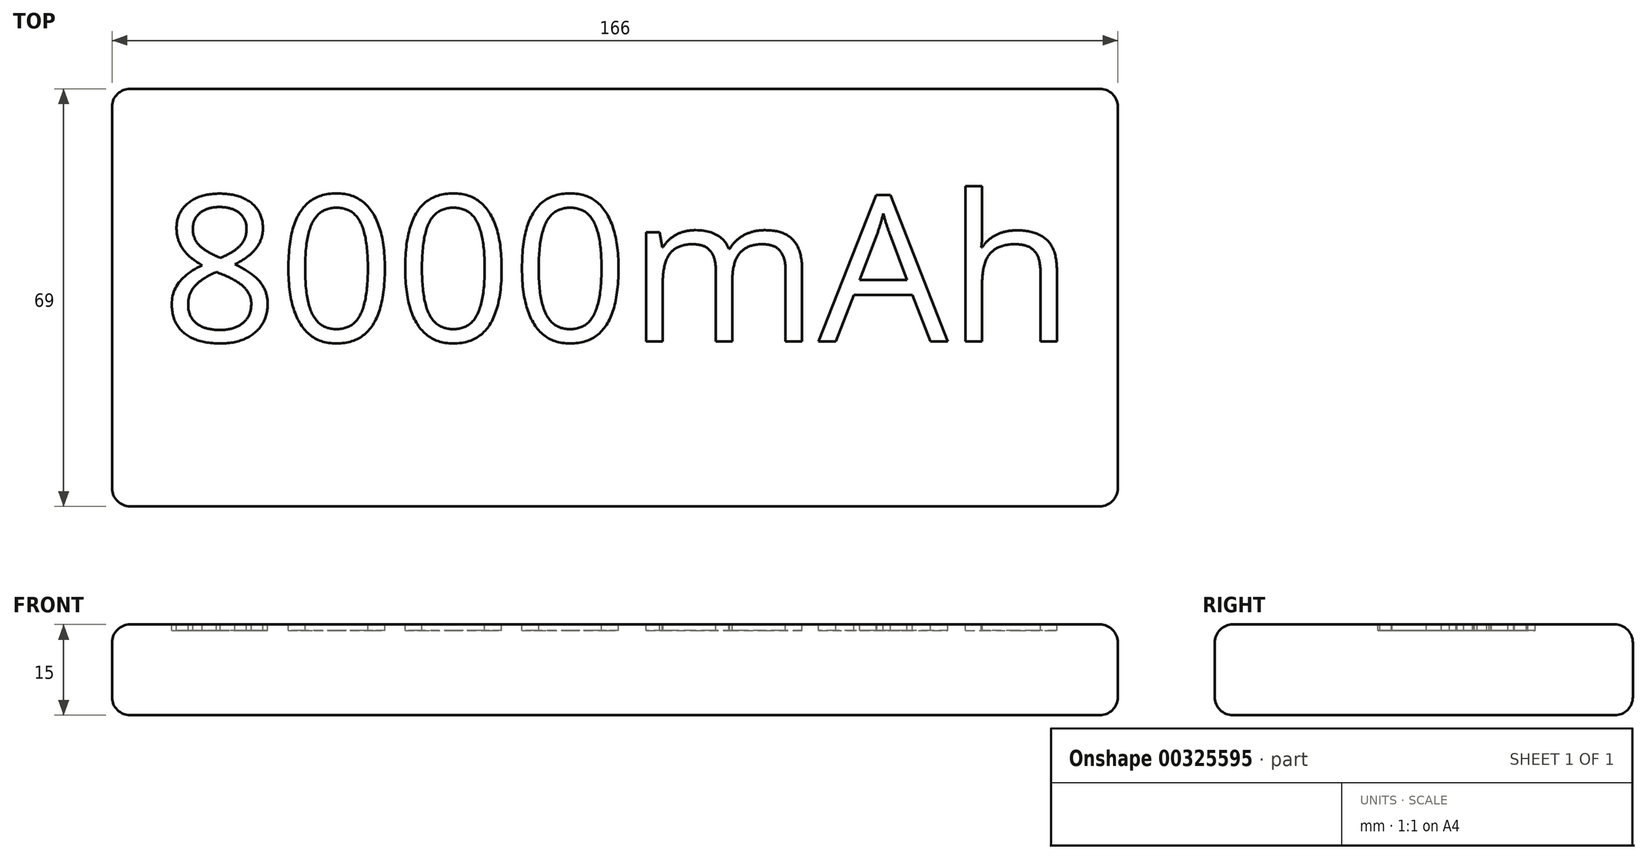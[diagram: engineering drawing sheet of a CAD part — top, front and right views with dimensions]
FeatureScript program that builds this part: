
annotation { "Feature Type Name" : "Feature", "Feature Type Description" : "" }
export const myFeature = defineFeature(function(context is Context, id is Id, definition is map)
    precondition{}
    {
        {
            var Q0;
            Q0=qCreatedBy(makeId("Top.planeOp"),FACE);
            var sketch = newSketch(context, id + "F0", { "sketchPlane" : qUnion([Q0])});
            skLineSegment(sketch, "E0.bottom", {"start": v(83, -34.5) * mm, "end": v(-83, -34.5) * mm});
            skLineSegment(sketch, "E0.top", {"start": v(83, 34.5) * mm, "end": v(-83, 34.5) * mm});
            skLineSegment(sketch, "E0.left", {"start": v(83, -34.5) * mm, "end": v(83, 34.5) * mm});
            skLineSegment(sketch, "E0.right", {"start": v(-83, -34.5) * mm, "end": v(-83, 34.5) * mm});
            skPoint(sketch, "E0.middle", {"position": v(0, 0) * mm});
            skSolve(sketch);
        }
        {
            var Q0;
            Q0 = qSketchRegion(id + "F0", true);
            extrude(context, id + "F1", {"entities" : qUnion([Q0]), "depth" : 15 * mm});
        }
        {
            var Q0;
            Q0=makeQuery(id+"F1.opExtrude","CAP_FACE",FACE,{"disambiguationData":[OSD([sQuery(id+"F0.wireOp",EDGE,"E0.bottom"),sQuery(id+"F0.wireOp",EDGE,"E0.top"),sQuery(id+"F0.wireOp",EDGE,"E0.left"),sQuery(id+"F0.wireOp",EDGE,"E0.right")])],"isStart":false});
            var Q1;
            Q1=makeQuery(id+"F1.opExtrude","CAP_FACE",FACE,{"disambiguationData":[OSD([sQuery(id+"F0.wireOp",EDGE,"E0.bottom"),sQuery(id+"F0.wireOp",EDGE,"E0.top"),sQuery(id+"F0.wireOp",EDGE,"E0.left"),sQuery(id+"F0.wireOp",EDGE,"E0.right")])],"isStart":true});
            var Q2;
            Q2=makeQuery(id+"F1.opExtrude","SWEPT_EDGE",EDGE,{"disambiguationData":[OSD([sQuery(id+"F0.wireOp",EDGE,"E0.bottom"),sQuery(id+"F0.wireOp",EDGE,"E0.right")])]});
            var Q3;
            Q3=makeQuery(id+"F1.opExtrude","SWEPT_EDGE",EDGE,{"disambiguationData":[OSD([sQuery(id+"F0.wireOp",EDGE,"E0.top"),sQuery(id+"F0.wireOp",EDGE,"E0.right")])]});
            var Q4;
            Q4=makeQuery(id+"F1.opExtrude","SWEPT_EDGE",EDGE,{"disambiguationData":[OSD([sQuery(id+"F0.wireOp",EDGE,"E0.bottom"),sQuery(id+"F0.wireOp",EDGE,"E0.left")])]});
            var Q5;
            Q5=makeQuery(id+"F1.opExtrude","SWEPT_EDGE",EDGE,{"disambiguationData":[OSD([sQuery(id+"F0.wireOp",EDGE,"E0.top"),sQuery(id+"F0.wireOp",EDGE,"E0.left")])]});
            fillet(context, id + "F2", {"entities" : qUnion([Q0, Q1, Q2, Q3, Q4, Q5]), "radius" : 3 * mm, "tangentPropagation" : true, "allowEdgeOverflow" : false});
        }
        {
            var Q0;
            Q0=makeQuery(id+"F1.opExtrude","CAP_FACE",FACE,{"disambiguationData":[OSD([sQuery(id+"F0.wireOp",EDGE,"E0.bottom"),sQuery(id+"F0.wireOp",EDGE,"E0.top"),sQuery(id+"F0.wireOp",EDGE,"E0.left"),sQuery(id+"F0.wireOp",EDGE,"E0.right")])],"isStart":false});
            var sketch = newSketch(context, id + "F3", { "sketchPlane" : qUnion([Q0])});
            skText(sketch, "E1", { "text": "8000mAh\n", "fontName": "OpenSans-Regular.ttf"});
            const initialGuessF3  = {"E1": [-0.07486, -0.00724, 1, 0, 0.02428]};
            skSetInitialGuess(sketch, initialGuessF3);
            skSolve(sketch);
        }
        {
            var Q0;
            Q0 = qSketchRegion(id + "F3", true);
            extrude(context, id + "F4", {"entities" : qUnion([Q0]), "operationType" : NewBodyOperationType.REMOVE, "oppositeDirection" : true, "depth" : 1 * mm});
        }
    });
